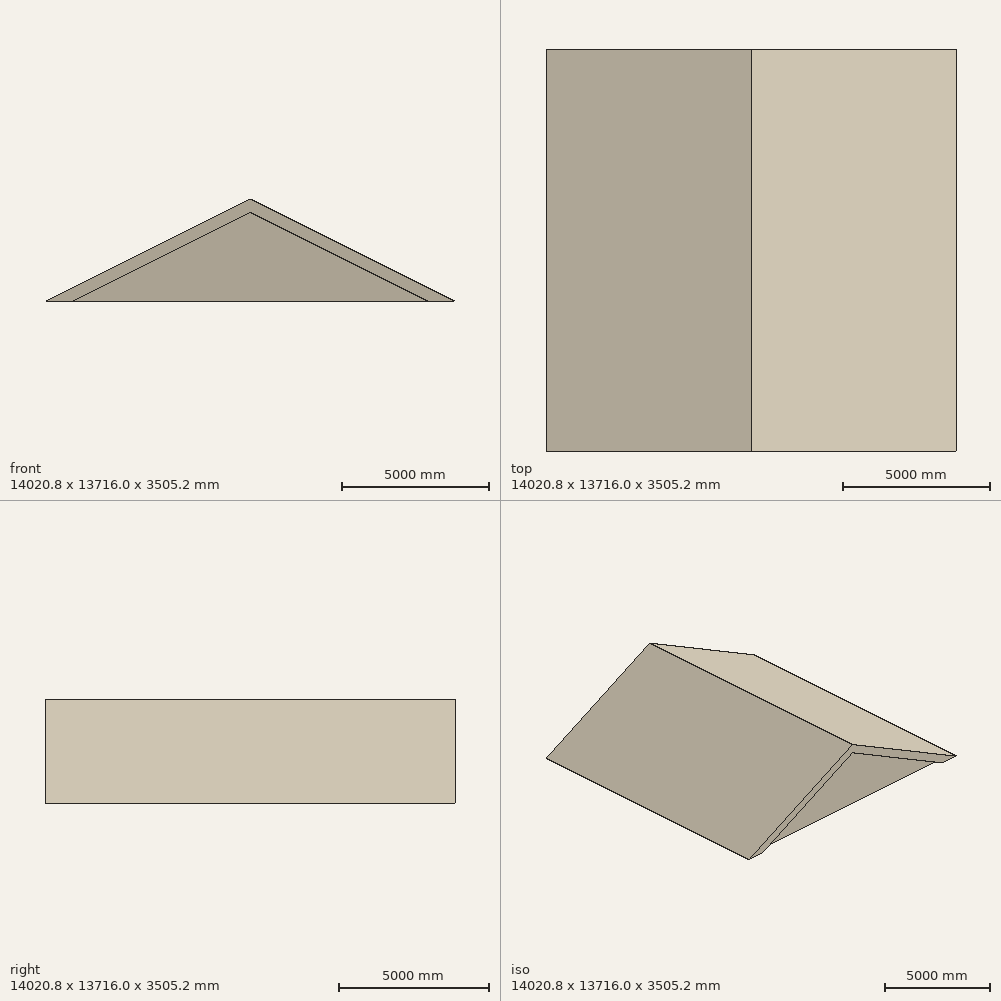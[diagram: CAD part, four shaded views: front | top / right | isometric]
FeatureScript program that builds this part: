
annotation { "Feature Type Name" : "Feature", "Feature Type Description" : "" }
export const myFeature = defineFeature(function(context is Context, id is Id, definition is map)
    precondition{}
    {
        {
            var Q0;
            Q0=qCreatedBy(makeId("Front.planeOp"),FACE);
            var sketch = newSketch(context, id + "F0", { "sketchPlane" : qUnion([Q0])});
            skLineSegment(sketch, "E0", {"start": v(0, 0) * mm, "end": v(-6096, 0) * mm});
            skLineSegment(sketch, "E1", {"start": v(0, 0) * mm, "end": v(6096, 0) * mm});
            skLineSegment(sketch, "E2", {"start": v(0, 0) * mm, "end": v(0, 3048) * mm, "construction": true});
            skLineSegment(sketch, "E3", {"start": v(-6096, 0) * mm, "end": v(0, 3048) * mm});
            skLineSegment(sketch, "E4", {"start": v(6096, 0) * mm, "end": v(0, 3048) * mm});
            skLineSegment(sketch, "E5", {"start": v(-6096, 0) * mm, "end": v(-7010.4, 0) * mm});
            skLineSegment(sketch, "E6", {"start": v(6096, 0) * mm, "end": v(7010.4, 0) * mm});
            skLineSegment(sketch, "E7", {"start": v(0, 3048) * mm, "end": v(0, 3505.2) * mm});
            skLineSegment(sketch, "E8", {"start": v(0, 3505.2) * mm, "end": v(7010.4, 0) * mm});
            skLineSegment(sketch, "E9", {"start": v(0, 3505.2) * mm, "end": v(-7010.4, 0) * mm});
            skLineSegment(sketch, "E10", {"start": v(-6096, 0) * mm, "end": v(-6096, -7315.2) * mm});
            skLineSegment(sketch, "E11", {"start": v(-6096, -7315.2) * mm, "end": v(6096, -7315.2) * mm});
            skLineSegment(sketch, "E12", {"start": v(6096, 0) * mm, "end": v(6096, -7315.2) * mm});
            skLineSegment(sketch, "E13", {"start": v(-6096, -7315.2) * mm, "end": v(-6096, -7620) * mm});
            skLineSegment(sketch, "E14", {"start": v(-6096, -7620) * mm, "end": v(6096, -7620) * mm});
            skLineSegment(sketch, "E15", {"start": v(6096, -7315.2) * mm, "end": v(6096, -7620) * mm});
            skLineSegment(sketch, "E16", {"start": v(0, 0) * mm, "end": v(0, -7315.2) * mm, "construction": true});
            skLineSegment(sketch, "E17", {"start": v(0, -7315.2) * mm, "end": v(-457.2, -7315.2) * mm});
            skLineSegment(sketch, "E18", {"start": v(-457.2, -7315.2) * mm, "end": v(-457.2, -5181.6) * mm});
            skLineSegment(sketch, "E19", {"start": v(-457.2, -5181.6) * mm, "end": v(457.2, -5181.6) * mm});
            skLineSegment(sketch, "E20", {"start": v(457.2, -5181.6) * mm, "end": v(457.2, -7315.2) * mm});
            skLineSegment(sketch, "E21", {"start": v(457.2, -7315.2) * mm, "end": v(-457.2, -7315.2) * mm});
            skLineSegment(sketch, "E22.bottom", {"start": v(2523.21, -5221.35) * mm, "end": v(4572, -5221.35) * mm});
            skLineSegment(sketch, "E22.top", {"start": v(2523.21, -6595.85) * mm, "end": v(4572, -6595.85) * mm});
            skLineSegment(sketch, "E22.left", {"start": v(2523.21, -5221.35) * mm, "end": v(2523.21, -6595.85) * mm});
            skLineSegment(sketch, "E22.right", {"start": v(4572, -5221.35) * mm, "end": v(4572, -6595.85) * mm});
            skLineSegment(sketch, "E23.0", {"start": v(2340.33, -5038.47) * mm, "end": v(4754.88, -5038.47) * mm});
            skLineSegment(sketch, "E23.1", {"start": v(2340.33, -5038.47) * mm, "end": v(2340.33, -6778.73) * mm});
            skLineSegment(sketch, "E23.2", {"start": v(2340.33, -6778.73) * mm, "end": v(4754.88, -6778.73) * mm});
            skLineSegment(sketch, "E23.3", {"start": v(4754.88, -5038.47) * mm, "end": v(4754.88, -6778.73) * mm});
            skLineSegment(sketch, "E24.bottom", {"start": v(-4572, -5221.22) * mm, "end": v(-2523.13, -5221.22) * mm});
            skLineSegment(sketch, "E24.top", {"start": v(-4572, -6595.87) * mm, "end": v(-2523.13, -6595.87) * mm});
            skLineSegment(sketch, "E24.left", {"start": v(-4572, -5221.22) * mm, "end": v(-4572, -6595.87) * mm});
            skLineSegment(sketch, "E24.right", {"start": v(-2523.13, -5221.22) * mm, "end": v(-2523.13, -6595.87) * mm});
            skLineSegment(sketch, "E25.0", {"start": v(-4754.88, -5038.34) * mm, "end": v(-2340.25, -5038.34) * mm});
            skLineSegment(sketch, "E25.1", {"start": v(-4754.88, -5038.34) * mm, "end": v(-4754.88, -6778.75) * mm});
            skLineSegment(sketch, "E25.2", {"start": v(-4754.88, -6778.75) * mm, "end": v(-2340.25, -6778.75) * mm});
            skLineSegment(sketch, "E25.3", {"start": v(-2340.25, -5038.34) * mm, "end": v(-2340.25, -6778.75) * mm});
            skSolve(sketch);
        }
        {
            var Q0;
            Q0=makeQuery(id+"F0.imprint","IMPRINT",FACE,{"disambiguationData":[TD([[makeQuery(id+"F0.imprint","IMPRINT",EDGE,{"derivedFrom":sQuery(id+"F0.wireOp",EDGE,"E3")}),1.0]])]});
            var Q1;
            Q1=makeQuery(id+"F0.imprint","IMPRINT",FACE,{"disambiguationData":[TD([[makeQuery(id+"F0.imprint","IMPRINT",EDGE,{"derivedFrom":sQuery(id+"F0.wireOp",EDGE,"E4")}),-1.0]])]});
            extrude(context, id + "F1", {"entities" : qUnion([Q0, Q1]), "endBound" : BoundingType.SYMMETRIC, "depth" : 13716 * mm, "offsetDistance" : 30.48 * mm});
        }
        {
            var Q0;
            Q0=makeQuery(id+"F0.imprint","IMPRINT",FACE,{"disambiguationData":[TD([[makeQuery(id+"F0.imprint","IMPRINT",EDGE,{"derivedFrom":sQuery(id+"F0.wireOp",EDGE,"E0")}),-1.0]])]});
            extrude(context, id + "F2", {"entities" : qUnion([Q0]), "operationType" : NewBodyOperationType.ADD, "endBound" : BoundingType.SYMMETRIC, "depth" : 13106.4 * mm, "offsetDistance" : 30.48 * mm});
        }
    });
